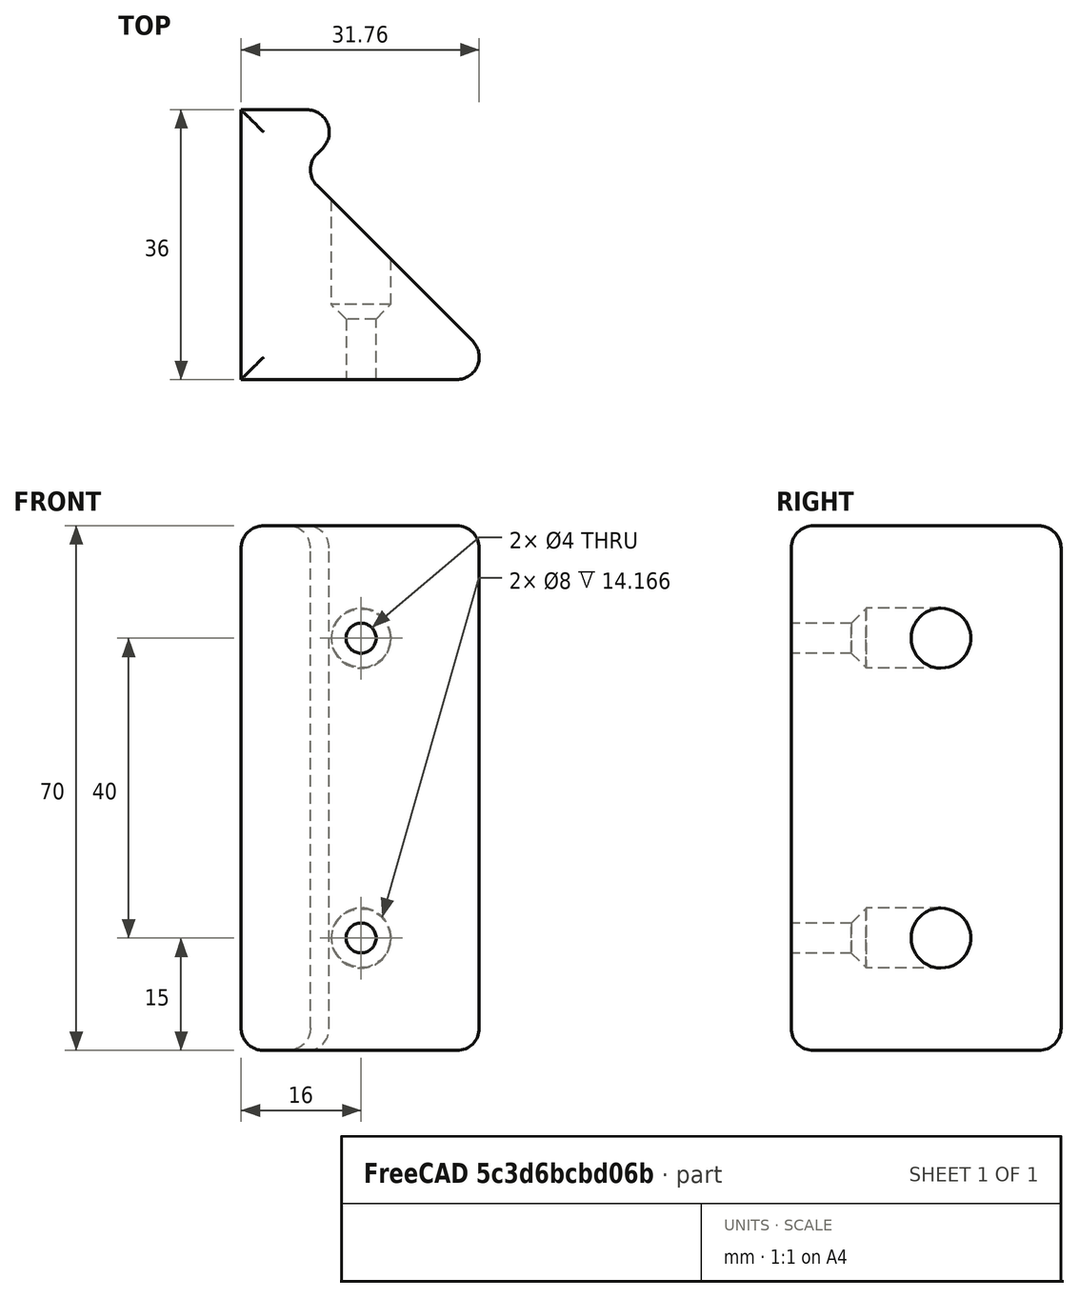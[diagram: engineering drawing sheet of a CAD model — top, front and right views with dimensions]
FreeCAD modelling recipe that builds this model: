
FCSTD DOCUMENT  (FreeCAD 0.20R)
Label: Butée_V1
License: All rights reserved
LicenseURL: http://en.wikipedia.org/wiki/All_rights_reserved
objects: Sketcher::SketchObject×3, PartDesign::Pad×2, PartDesign::Fillet×1, PartDesign::Pocket×1, PartDesign::Chamfer×1, PartDesign::Body×1, Mesh::Feature×1
note: 14 computed .brp shape members not serialized (recipe doc carries the construction recipe); baked Part::Feature solids carry a one-line shape summary decoded from their .brp

FEATURE [Sketcher::SketchObject] Sketch
  FullyConstrained = true
  MapMode = 5
  Support = -> [XY_Plane]
  sketch-geometry (5):
    g0: LineSegment StartX=0 StartY=0 StartZ=0 EndX=0 EndY=36 EndZ=0
    g1: LineSegment StartX=0 StartY=36 StartZ=0 EndX=16 EndY=36 EndZ=0
    g2: LineSegment StartX=16 StartY=36 StartZ=0 EndX=8 EndY=28 EndZ=0
    g3: LineSegment StartX=8 StartY=28 StartZ=0 EndX=36 EndY=0 EndZ=0
    g4: LineSegment StartX=36 StartY=0 StartZ=0 EndX=0 EndY=0 EndZ=0
  constraints (14):
    c: Coincident(g-1,g0)
    c: PointOnObject(g0,g-2)
    c: Coincident(g0,g1)
    c: Horizontal(g1)
    c: Coincident(g1,g2)
    c: Coincident(g2,g3)
    c: PointOnObject(g3,g-1)
    c: Coincident(g3,g4)
    c: Coincident(g4,g0)
    c: DistanceX(g4,g4) = 36
    c: DistanceY(g0,g0) = 36
    c: Angle(g3,g4) = 0.785398
    c: Distance(g2,g0) = 8
    c: Perpendicular(g2,g3)
FEATURE [PartDesign::Pad] Pad
  Direction = (0,0,1)
  Length = 70
  Length2 = 100
  Profile = -> Sketch
  Type = 0
FEATURE [PartDesign::Fillet] Fillet
  Base = -> Pad [Face7,Face6,Edge5,Edge8,Edge11]
  BaseFeature = -> Pad
  Radius = 3
  SupportTransform = false
FEATURE [Sketcher::SketchObject] Sketch001
  ExternalGeometry = -> [Fillet]
  FullyConstrained = true
  MapMode = 5
  Placement = pos=(0,0,0) rot=(1,0,0;1.5708rad)
  Support = -> [Fillet]
  sketch-geometry (2):
    g0: Circle CenterX=16 CenterY=55 CenterZ=0 NormalX=0 NormalY=0 NormalZ=1 AngleXU=0 Radius=4
    g1: Circle CenterX=16 CenterY=15 CenterZ=0 NormalX=0 NormalY=0 NormalZ=1 AngleXU=0 Radius=4
  constraints (6):
    c: Distance(g0,g-3) = 15
    c: DistanceY(g-1,g1) = 15
    c: Radius(g0) = 4
    c: Equal(g0,g1)
    c: DistanceX(g-2,g0) = 16
    c: DistanceX(g-2,g1) = 16
FEATURE [PartDesign::Pocket] Pocket
  BaseFeature = -> Fillet
  Length = 30
  Length2 = 100
  Profile = -> Sketch001
  Type = 0
FEATURE [Sketcher::SketchObject] Sketch002
  ExternalGeometry = -> [Pocket]
  FullyConstrained = true
  MapMode = 5
  Placement = pos=(0,0,0) rot=(1,0,0;1.5708rad)
  Support = -> [Pocket]
  sketch-geometry (4):
    g0: Circle CenterX=16 CenterY=55 CenterZ=0 NormalX=0 NormalY=0 NormalZ=1 AngleXU=0 Radius=2
    g1: Circle CenterX=16 CenterY=55 CenterZ=0 NormalX=0 NormalY=0 NormalZ=1 AngleXU=0 Radius=6
    g2: Circle CenterX=16 CenterY=15 CenterZ=0 NormalX=0 NormalY=0 NormalZ=1 AngleXU=0 Radius=2
    g3: Circle CenterX=16 CenterY=15 CenterZ=0 NormalX=0 NormalY=0 NormalZ=1 AngleXU=0 Radius=6
  constraints (8):
    c: Coincident(g0,g-3)
    c: Coincident(g1,g0)
    c: Coincident(g2,g-4)
    c: Coincident(g3,g2)
    c: Radius(g3) = 6
    c: Equal(g3,g1)
    c: Radius(g2) = 2
    c: Equal(g2,g0)
FEATURE [PartDesign::Pad] Pad001
  BaseFeature = -> Pocket
  Direction = (0,-1,2e-16)
  Length = 10
  Length2 = 100
  Profile = -> Sketch002
  Reversed = true
  Type = 0
FEATURE [PartDesign::Chamfer] Chamfer
  Angle = 45
  Base = -> Pad001 [Edge72,Edge70]
  BaseFeature = -> Pad001
  ChamferType = 0
  FlipDirection = false
  Size = 1.95
  Size2 = 1
  SupportTransform = false
FEATURE [PartDesign::Body] Body  label="Poignée"
  Group = -> [Sketch,Pad,Fillet,Sketch001,Pocket,Sketch002,Pad001,Chamfer]
  Origin = -> Origin
  Tip = -> Chamfer
FEATURE [Mesh::Feature] Mesh  label="Poignée (Meshed)"
